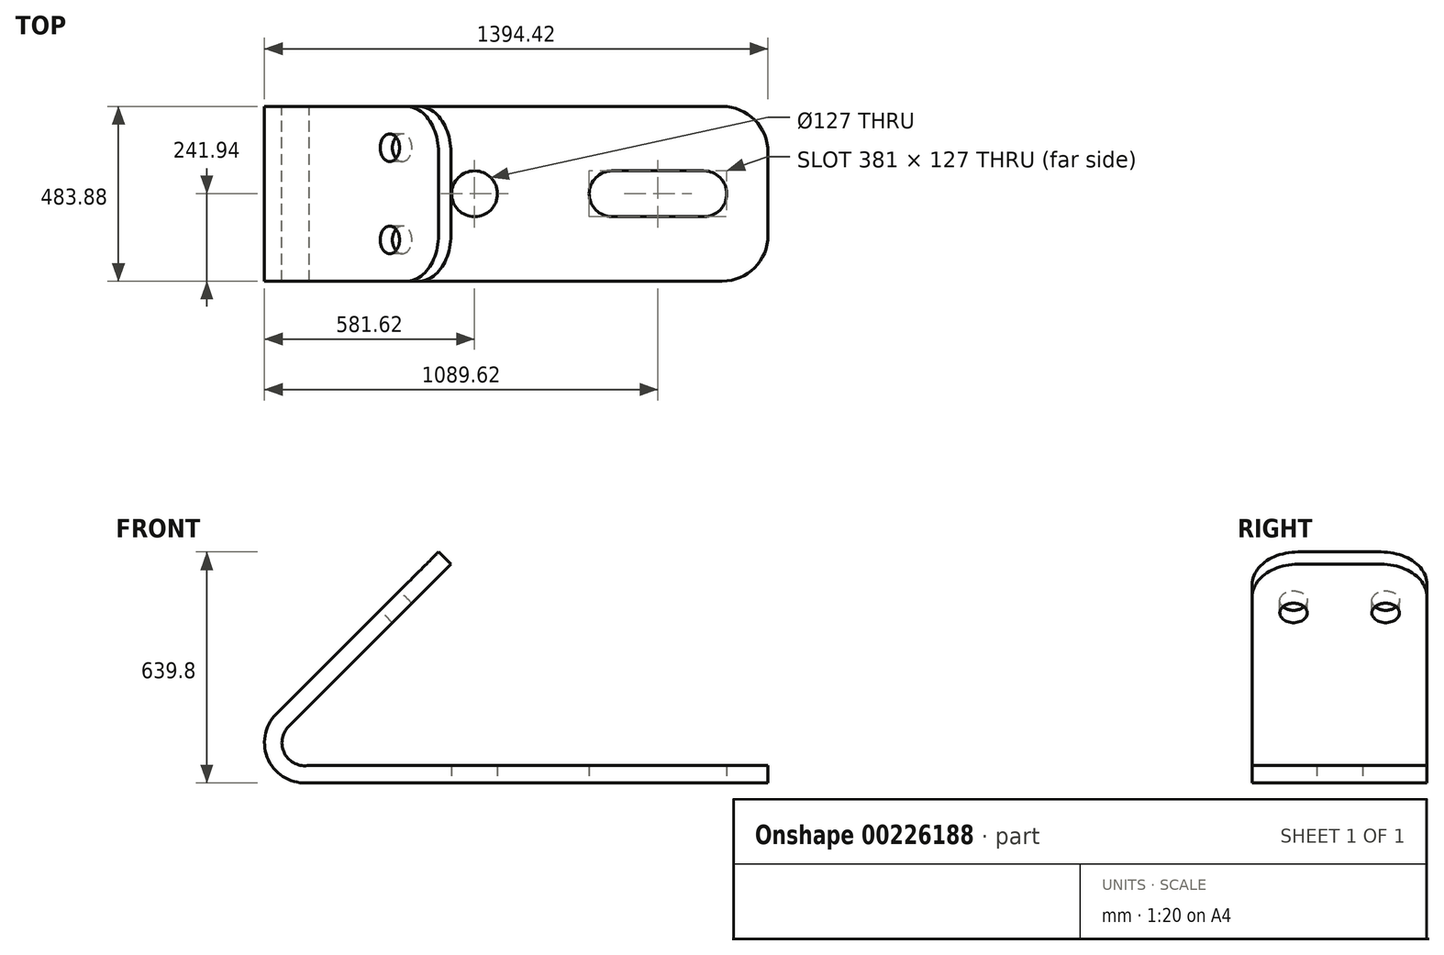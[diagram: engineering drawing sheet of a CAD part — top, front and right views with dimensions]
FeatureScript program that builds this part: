
annotation { "Feature Type Name" : "Feature", "Feature Type Description" : "" }
export const myFeature = defineFeature(function(context is Context, id is Id, definition is map)
    precondition{}
    {
        {
            var Q0;
            Q0=qCreatedBy(makeId("Top.planeOp"),FACE);
            var sketch = newSketch(context, id + "F0", { "sketchPlane" : qUnion([Q0])});
            skLineSegment(sketch, "E0.bottom", {"start": v(635, -241.94) * mm, "end": v(-635, -241.94) * mm});
            skLineSegment(sketch, "E0.top", {"start": v(635, 241.94) * mm, "end": v(-635, 241.93) * mm});
            skLineSegment(sketch, "E0.left", {"start": v(635, -241.94) * mm, "end": v(635, 241.94) * mm});
            skLineSegment(sketch, "E0.right", {"start": v(-635, -241.94) * mm, "end": v(-635, 241.93) * mm});
            skPoint(sketch, "E0.middle", {"position": v(0, 0) * mm});
            skCircle(sketch, "E1", {"center": v(-177.8, 0) * mm, "radius": 63.5 * mm});
            skCircle(sketch, "E2", {"center": v(203.2, 0) * mm, "radius": 63.5 * mm});
            skCircle(sketch, "E3", {"center": v(457.2, 0) * mm, "radius": 63.5 * mm});
            skLineSegment(sketch, "E4", {"start": v(203.2, 63.5) * mm, "end": v(457.2, 63.5) * mm});
            skLineSegment(sketch, "E5", {"start": v(457.2, -63.5) * mm, "end": v(203.2, -63.5) * mm});
            skSolve(sketch);
        }
        {
            var Q0;
            Q0 = qSketchRegion(id + "F0", true);
            extrude(context, id + "F1", {"entities" : qUnion([Q0]), "depth" : 48.26 * mm});
        }
        {
            var Q0;
            Q0=makeQuery(id+"F1.opExtrude","SWEPT_EDGE",EDGE,{"disambiguationData":[OSD([sQuery(id+"F0.wireOp",EDGE,"E0.bottom"),sQuery(id+"F0.wireOp",EDGE,"E0.left")])]});
            var Q1;
            Q1=makeQuery(id+"F1.opExtrude","SWEPT_EDGE",EDGE,{"disambiguationData":[OSD([sQuery(id+"F0.wireOp",EDGE,"E0.top"),sQuery(id+"F0.wireOp",EDGE,"E0.left")])]});
            fillet(context, id + "F2", {"entities" : qUnion([Q0, Q1]), "radius" : 127 * mm, "tangentPropagation" : true, "allowEdgeOverflow" : false});
        }
        {
            var Q0;
            Q0=qCreatedBy(makeId("Front.planeOp"),FACE);
            var sketch = newSketch(context, id + "F3", { "sketchPlane" : qUnion([Q0])});
            skPoint(sketch, "E6.0", {"position": v(-635, 0) * mm});
            skLineSegment(sketch, "E7.0", {"start": v(-635, 48.26) * mm, "end": v(-635, 0) * mm});
            skLineSegment(sketch, "E8.0.0", {"start": v(-635, 0) * mm, "end": v(508, 0) * mm});
            skLineSegment(sketch, "E8.0.1", {"start": v(508, 0) * mm, "end": v(508, 48.26) * mm});
            skLineSegment(sketch, "E8.0.2", {"start": v(508, 48.26) * mm, "end": v(-635, 48.26) * mm});
            skArc(sketch, "E9", {"start": v(-726.69, 190.07) * mm, "mid": v(-748.32, 62.48) * mm, "end": v(-635, 0) * mm});
            skLineSegment(sketch, "E10", {"start": v(-726.69, 190.07) * mm, "end": v(-277.67, 639.08) * mm});
            skLineSegment(sketch, "E11", {"start": v(-277.67, 639.08) * mm, "end": v(-243.55, 604.95) * mm});
            skLineSegment(sketch, "E12", {"start": v(-243.55, 604.95) * mm, "end": v(-692.56, 155.94) * mm});
            skLineSegment(sketch, "E13", {"start": v(-692.56, 155.94) * mm, "end": v(-726.69, 190.07) * mm});
            skArc(sketch, "E14", {"start": v(-692.56, 155.94) * mm, "mid": v(-703.71, 80.76) * mm, "end": v(-635, 48.26) * mm});
            skSolve(sketch);
        }
        {
            var Q0;
            Q0=makeQuery(id+"F3.imprint","IMPRINT",FACE,{"disambiguationData":[TD([[makeQuery(id+"F3.imprint","IMPRINT",EDGE,{"derivedFrom":sQuery(id+"F3.wireOp",EDGE,"E10")}),-1.0]])]});
            var Q1;
            Q1=makeQuery(id+"F3.imprint","IMPRINT",FACE,{"disambiguationData":[TD([[makeQuery(id+"F3.imprint","IMPRINT",EDGE,{"derivedFrom":sQuery(id+"F3.wireOp",EDGE,"E7.0")}),-1.0]])]});
            extrude(context, id + "F4", {"entities" : qUnion([Q0, Q1]), "operationType" : NewBodyOperationType.ADD, "endBound" : BoundingType.SYMMETRIC, "depth" : 483.87 * mm});
        }
        {
            var Q0;
            Q0=makeQuery(id+"F4.opExtrude","CAP_EDGE",EDGE,{"disambiguationData":[OSD([sQuery(id+"F3.wireOp",EDGE,"E11")])],"isStart":true});
            var Q1;
            Q1=makeQuery(id+"F4.opExtrude","CAP_EDGE",EDGE,{"disambiguationData":[OSD([sQuery(id+"F3.wireOp",EDGE,"E11")])],"isStart":false});
            fillet(context, id + "F5", {"entities" : qUnion([Q0, Q1]), "radius" : 127 * mm, "tangentPropagation" : true, "allowEdgeOverflow" : false});
        }
        {
            var Q0;
            Q0=makeQuery(id+"F4.opExtrude","SWEPT_FACE",FACE,{"disambiguationData":[OSD([sQuery(id+"F3.wireOp",EDGE,"E10")])]});
            var sketch = newSketch(context, id + "F6", { "sketchPlane" : qUnion([Q0])});
            skCircle(sketch, "E15", {"center": v(-127.64, 65.05) * mm, "radius": 38.1 * mm});
            skCircle(sketch, "E16", {"center": v(127.64, 65.05) * mm, "radius": 38.1 * mm});
            skLineSegment(sketch, "E17", {"start": v(-127.64, 65.05) * mm, "end": v(127.64, 65.05) * mm});
            skSolve(sketch);
        }
        {
            var Q0;
            Q0 = qSketchRegion(id + "F6", true);
            extrude(context, id + "F7", {"entities" : qUnion([Q0]), "operationType" : NewBodyOperationType.REMOVE, "oppositeDirection" : true, "depth" : 48.26 * mm});
        }
    });
